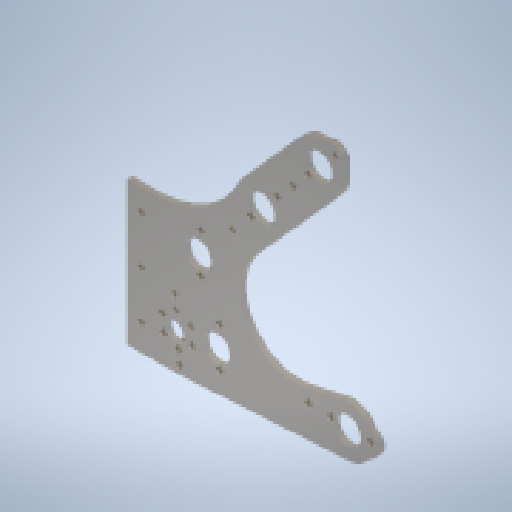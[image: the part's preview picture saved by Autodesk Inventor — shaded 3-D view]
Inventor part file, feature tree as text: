
AUTODESK INVENTOR PART (.ipt)
format: ipt  version: 2023.4 (Build 274418000, 418)  size: 382,976 bytes
history: native  units: in
note: dims shown in document units (in); Inventor stores cm internally (conversion verified against a paired STEP export)
features: sketch x2, extrude x1, hole x1, fillet x1
ambient origin geometry x8: Origin, YZ Plane, XZ Plane, XY Plane, X Axis, Y Axis, Z Axis, Center Point
bodies: Body1 (feature_tree)
feature tree (5):
  sketch  "Sketch1"  dims[d0=4.0in d2=3.0in]
  sketch  "Sketch4"  dims[d3=3.0in d4=3.0in d8=16.0in d9=12.0in d11=12.0in d13=4.5in d14=4.25in d15=0.5in d16=3.642in d17=60.0deg d63=1.125in d64=3.125in d65=1.88in d66=5.499in d67=4.018in d68=0.4688in d69=2.0in d70=0.5in d71=0.0172in d72=0.5841in d73=1.0in d74=6.0in d75=4.0in d76=1.655in d77=0.5in d79=1.0in d80=0.75in d81=1.375in d82=0.25in d83=0.0in d84=0.201in d85=0.75in d86=0.375in d87=0.25in d88=0.5635in d89=1.0in d90=0.8108in d91=1.0in d92=0.5in d93=2.3622in d95=360.0deg]
  extrude  "Extrusion2"  Depth=3.0in
  hole  "Hole2"  [1 undecoded]
  fillet  "Fillet2"  Radius=16.0in
note: 1 required parameter value undecoded (feature->parameter linkage not recoverable at this tier; creation-order binding heuristic only, values carry confidence <= 0.55)
